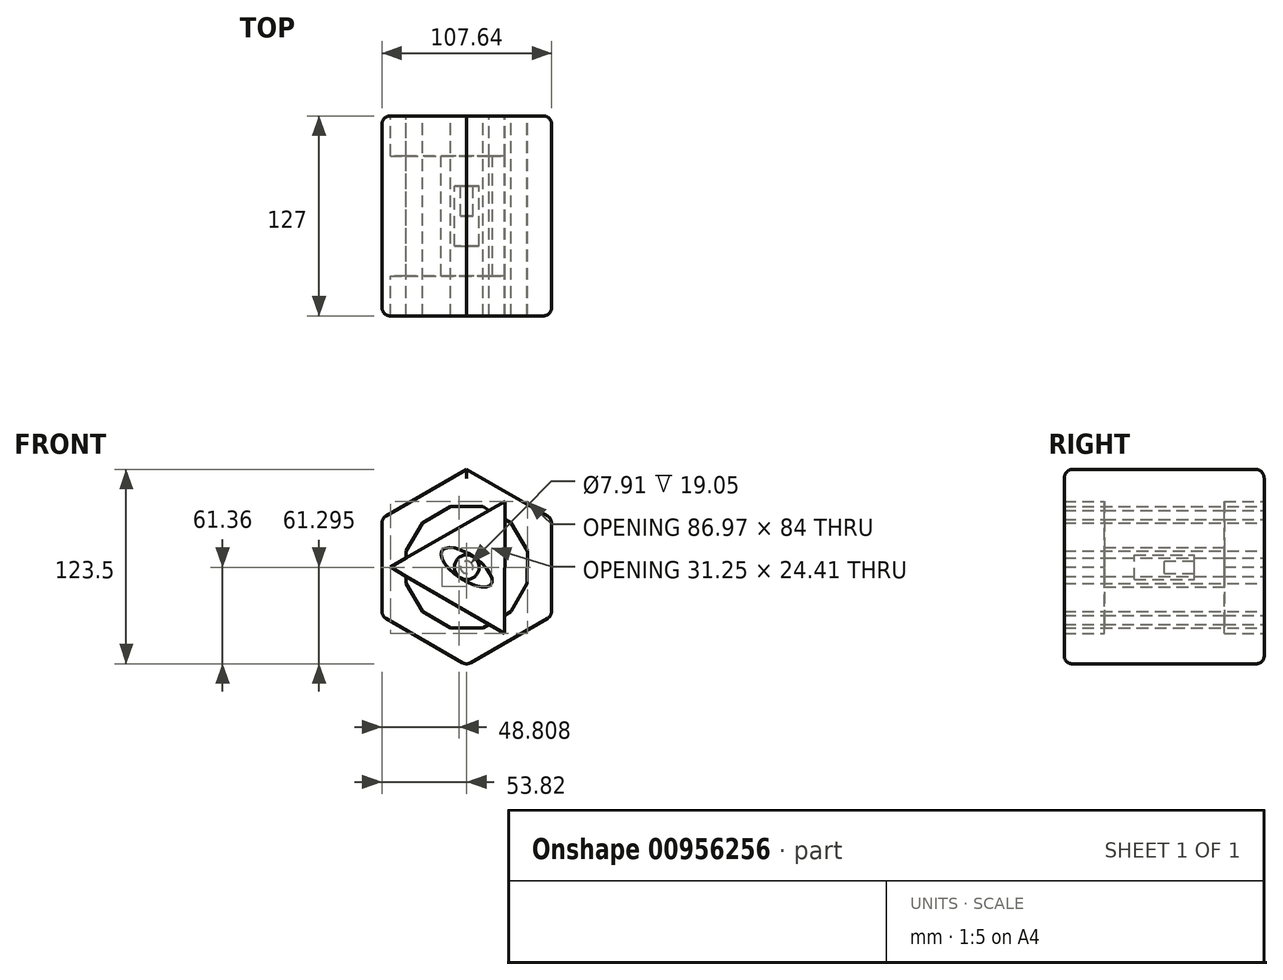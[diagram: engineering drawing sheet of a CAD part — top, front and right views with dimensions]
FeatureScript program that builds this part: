
annotation { "Feature Type Name" : "Feature", "Feature Type Description" : "" }
export const myFeature = defineFeature(function(context is Context, id is Id, definition is map)
    precondition{}
    {
        {
            var Q0;
            Q0=qCreatedBy(makeId("Front.planeOp"),FACE);
            var sketch = newSketch(context, id + "F0", { "sketchPlane" : qUnion([Q0])});
            skCircle(sketch, "E0.cCircle", {"center": v(0, 0) * mm, "radius": 53.82 * mm, "construction": true});
            skLineSegment(sketch, "E0.0", {"start": v(-53.82, -31.07) * mm, "end": v(-53.82, 31.07) * mm});
            skLineSegment(sketch, "E0.1", {"start": v(-53.82, 31.07) * mm, "end": v(0, 62.14) * mm});
            skLineSegment(sketch, "E0.2", {"start": v(0, 62.14) * mm, "end": v(53.82, 31.07) * mm});
            skLineSegment(sketch, "E0.3", {"start": v(53.82, 31.07) * mm, "end": v(53.82, -31.07) * mm});
            skLineSegment(sketch, "E0.4", {"start": v(53.82, -31.07) * mm, "end": v(0, -62.14) * mm});
            skLineSegment(sketch, "E0.5", {"start": v(0, -62.14) * mm, "end": v(-53.82, -31.07) * mm});
            skPoint(sketch, "E0.0.midPoint", {"position": v(-53.82, 0) * mm});
            skCircle(sketch, "E1.cCircle", {"center": v(0, 0) * mm, "radius": 38.46 * mm, "construction": true});
            skLineSegment(sketch, "E1.0", {"start": v(-28.12, 28.19) * mm, "end": v(-10.26, 38.47) * mm});
            skLineSegment(sketch, "E1.1", {"start": v(-10.26, 38.47) * mm, "end": v(10.35, 38.45) * mm});
            skLineSegment(sketch, "E1.2", {"start": v(10.35, 38.45) * mm, "end": v(28.19, 28.12) * mm});
            skLineSegment(sketch, "E1.3", {"start": v(28.19, 28.12) * mm, "end": v(38.47, 10.26) * mm});
            skLineSegment(sketch, "E1.4", {"start": v(38.47, 10.26) * mm, "end": v(38.45, -10.35) * mm});
            skLineSegment(sketch, "E1.5", {"start": v(38.45, -10.35) * mm, "end": v(28.12, -28.19) * mm});
            skLineSegment(sketch, "E1.6", {"start": v(28.12, -28.19) * mm, "end": v(10.26, -38.47) * mm});
            skLineSegment(sketch, "E1.7", {"start": v(10.26, -38.47) * mm, "end": v(-10.35, -38.45) * mm});
            skLineSegment(sketch, "E1.8", {"start": v(-10.35, -38.45) * mm, "end": v(-28.19, -28.12) * mm});
            skLineSegment(sketch, "E1.9", {"start": v(-28.19, -28.12) * mm, "end": v(-38.47, -10.26) * mm});
            skLineSegment(sketch, "E1.10", {"start": v(-38.47, -10.26) * mm, "end": v(-38.45, 10.35) * mm});
            skLineSegment(sketch, "E1.11", {"start": v(-38.45, 10.35) * mm, "end": v(-28.12, 28.19) * mm});
            skPoint(sketch, "E1.0.midPoint", {"position": v(-19.19, 33.33) * mm});
            skCircle(sketch, "E2.cCircle", {"center": v(0, 0) * mm, "radius": 24.25 * mm, "construction": true});
            skLineSegment(sketch, "E2.0", {"start": v(-48.5, 0.13) * mm, "end": v(24.36, 41.93) * mm});
            skLineSegment(sketch, "E2.1", {"start": v(24.36, 41.93) * mm, "end": v(24.13, -42.06) * mm});
            skLineSegment(sketch, "E2.2", {"start": v(24.13, -42.06) * mm, "end": v(-48.5, 0.13) * mm});
            skPoint(sketch, "E2.0.midPoint", {"position": v(-12.07, 21.03) * mm});
            skEllipse(sketch, "E3", {"center": v(0, 0) * mm, "majorRadius": 18.93 * mm, "minorRadius": 7.98 * mm, "majorAxis": v(-0.83, 0.56)});
            skCircle(sketch, "E4", {"center": v(0, 0) * mm, "radius": 7.87 * mm});
            skCircle(sketch, "E5", {"center": v(0, 0) * mm, "radius": 3.96 * mm});
            skSolve(sketch);
        }
        {
            var Q0;
            Q0=makeQuery(id+"F0.imprint","IMPRINT",FACE,{"disambiguationData":[TD([[makeQuery(id+"F0.imprint","IMPRINT",EDGE,{"derivedFrom":sQuery(id+"F0.wireOp",EDGE,"E0.0")}),-1.0]])]});
            extrude(context, id + "F1", {"entities" : qUnion([Q0]), "endBound" : BoundingType.SYMMETRIC, "depth" : 127 * mm, "offsetDistance" : 25.4 * mm});
        }
        {
            var Q0;
            {var subQ0=sQuery(id+"F0.wireOp",EDGE,"E2.0");var subQ1=sQuery(id+"F0.wireOp",EDGE,"E1.2");var subQ2=makeQuery(id+"F0.imprint","INTERSECT",VERTEX,{"derivedFrom":[subQ1,subQ0]});Q0=makeQuery(id+"F0.imprint","IMPRINT",FACE,{"disambiguationData":[TD([[makeQuery(id+"F0.imprint","IMPRINT",EDGE,{"disambiguationData":[TD([[subQ2,-1.0]])],"derivedFrom":subQ1}),1.0]])]});}
            var Q1;
            {var subQ0=sQuery(id+"F0.wireOp",EDGE,"E2.2");var subQ1=sQuery(id+"F0.wireOp",EDGE,"E1.10");var subQ2=makeQuery(id+"F0.imprint","INTERSECT",VERTEX,{"derivedFrom":[subQ1,subQ0]});Q1=makeQuery(id+"F0.imprint","IMPRINT",FACE,{"disambiguationData":[TD([[makeQuery(id+"F0.imprint","IMPRINT",EDGE,{"disambiguationData":[TD([[subQ2,-1.0]])],"derivedFrom":subQ1}),1.0]])]});}
            var Q2;
            {var subQ0=sQuery(id+"F0.wireOp",EDGE,"E2.1");var subQ1=sQuery(id+"F0.wireOp",EDGE,"E1.6");var subQ2=makeQuery(id+"F0.imprint","INTERSECT",VERTEX,{"derivedFrom":[subQ1,subQ0]});Q2=makeQuery(id+"F0.imprint","IMPRINT",FACE,{"disambiguationData":[TD([[makeQuery(id+"F0.imprint","IMPRINT",EDGE,{"disambiguationData":[TD([[subQ2,-1.0]])],"derivedFrom":subQ1}),1.0]])]});}
            var Q3;
            Q3=makeQuery(id+"F0.imprint","IMPRINT",FACE,{"disambiguationData":[TD([[makeQuery(id+"F0.imprint","IMPRINT",EDGE,{"derivedFrom":sQuery(id+"F0.wireOp",EDGE,"E3")}),-1.0]])]});
            extrude(context, id + "F2", {"entities" : qUnion([Q0, Q1, Q2, Q3]), "operationType" : NewBodyOperationType.ADD, "endBound" : BoundingType.SYMMETRIC, "depth" : 76.2 * mm, "offsetDistance" : 25.4 * mm});
        }
        {
            var Q0;
            Q0=makeQuery(id+"F0.imprint","IMPRINT",FACE,{"disambiguationData":[TD([[makeQuery(id+"F0.imprint","IMPRINT",EDGE,{"derivedFrom":sQuery(id+"F0.wireOp",EDGE,"E4")}),1.0]])]});
            extrude(context, id + "F3", {"entities" : qUnion([Q0]), "endBound" : BoundingType.SYMMETRIC, "depth" : 38.1 * mm, "offsetDistance" : 25.4 * mm});
        }
        {
            var Q0;
            Q0=makeQuery(id+"F0.imprint","IMPRINT",FACE,{"disambiguationData":[TD([[makeQuery(id+"F0.imprint","IMPRINT",EDGE,{"derivedFrom":sQuery(id+"F0.wireOp",EDGE,"E5")}),1.0]])]});
            extrude(context, id + "F4", {"entities" : qUnion([Q0]), "operationType" : NewBodyOperationType.ADD, "depth" : 19.05 * mm, "offsetDistance" : 25.4 * mm});
        }
        {
            var Q0;
            Q0=makeQuery(id+"F1.opExtrude","SWEPT_EDGE",EDGE,{"disambiguationData":[OSD([sQuery(id+"F0.wireOp",EDGE,"E0.2"),sQuery(id+"F0.wireOp",EDGE,"E0.3")])]});
            var Q1;
            Q1=makeQuery(id+"F1.opExtrude","SWEPT_EDGE",EDGE,{"disambiguationData":[OSD([sQuery(id+"F0.wireOp",EDGE,"E0.3"),sQuery(id+"F0.wireOp",EDGE,"E0.4")])]});
            var Q2;
            Q2=makeQuery(id+"F1.opExtrude","SWEPT_EDGE",EDGE,{"disambiguationData":[OSD([sQuery(id+"F0.wireOp",EDGE,"E0.4"),sQuery(id+"F0.wireOp",EDGE,"E0.5")])]});
            var Q3;
            Q3=makeQuery(id+"F1.opExtrude","SWEPT_EDGE",EDGE,{"disambiguationData":[OSD([sQuery(id+"F0.wireOp",EDGE,"E0.0"),sQuery(id+"F0.wireOp",EDGE,"E0.5")])]});
            var Q4;
            Q4=makeQuery(id+"F1.opExtrude","SWEPT_EDGE",EDGE,{"disambiguationData":[OSD([sQuery(id+"F0.wireOp",EDGE,"E0.0"),sQuery(id+"F0.wireOp",EDGE,"E0.1")])]});
            var Q5;
            Q5=makeQuery(id+"F1.opExtrude","CAP_EDGE",EDGE,{"disambiguationData":[OSD([sQuery(id+"F0.wireOp",EDGE,"E0.1")])],"isStart":false});
            var Q6;
            Q6=makeQuery(id+"F1.opExtrude","CAP_EDGE",EDGE,{"disambiguationData":[OSD([sQuery(id+"F0.wireOp",EDGE,"E0.0")])],"isStart":false});
            var Q7;
            Q7=makeQuery(id+"F1.opExtrude","CAP_EDGE",EDGE,{"disambiguationData":[OSD([sQuery(id+"F0.wireOp",EDGE,"E0.5")])],"isStart":false});
            var Q8;
            Q8=makeQuery(id+"F1.opExtrude","CAP_EDGE",EDGE,{"disambiguationData":[OSD([sQuery(id+"F0.wireOp",EDGE,"E0.4")])],"isStart":false});
            var Q9;
            Q9=makeQuery(id+"F1.opExtrude","CAP_EDGE",EDGE,{"disambiguationData":[OSD([sQuery(id+"F0.wireOp",EDGE,"E0.3")])],"isStart":false});
            var Q10;
            Q10=makeQuery(id+"F1.opExtrude","CAP_EDGE",EDGE,{"disambiguationData":[OSD([sQuery(id+"F0.wireOp",EDGE,"E0.2")])],"isStart":false});
            var Q11;
            Q11=makeQuery(id+"F1.opExtrude","CAP_EDGE",EDGE,{"disambiguationData":[OSD([sQuery(id+"F0.wireOp",EDGE,"E0.2")])],"isStart":true});
            var Q12;
            Q12=makeQuery(id+"F1.opExtrude","CAP_EDGE",EDGE,{"disambiguationData":[OSD([sQuery(id+"F0.wireOp",EDGE,"E0.1")])],"isStart":true});
            var Q13;
            Q13=makeQuery(id+"F1.opExtrude","CAP_EDGE",EDGE,{"disambiguationData":[OSD([sQuery(id+"F0.wireOp",EDGE,"E0.3")])],"isStart":true});
            var Q14;
            Q14=makeQuery(id+"F1.opExtrude","CAP_EDGE",EDGE,{"disambiguationData":[OSD([sQuery(id+"F0.wireOp",EDGE,"E0.4")])],"isStart":true});
            var Q15;
            Q15=makeQuery(id+"F1.opExtrude","CAP_EDGE",EDGE,{"disambiguationData":[OSD([sQuery(id+"F0.wireOp",EDGE,"E0.5")])],"isStart":true});
            var Q16;
            Q16=makeQuery(id+"F1.opExtrude","CAP_EDGE",EDGE,{"disambiguationData":[OSD([sQuery(id+"F0.wireOp",EDGE,"E0.0")])],"isStart":true});
            fillet(context, id + "F5", {"entities" : qUnion([Q0, Q1, Q2, Q3, Q4, Q5, Q6, Q7, Q8, Q9, Q10, Q11, Q12, Q13, Q14, Q15, Q16]), "radius" : 5.08 * mm, "tangentPropagation" : true, "allowEdgeOverflow" : false});
        }
    });
